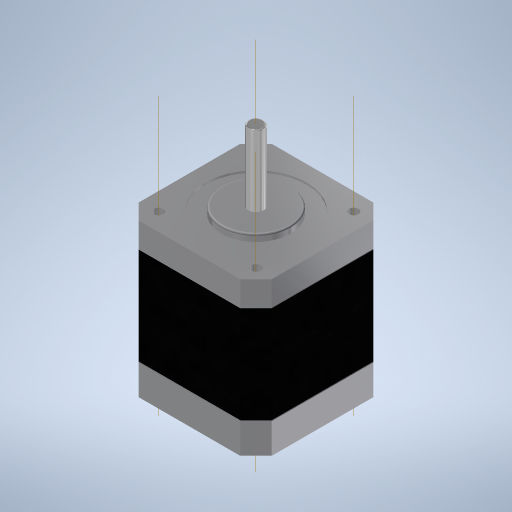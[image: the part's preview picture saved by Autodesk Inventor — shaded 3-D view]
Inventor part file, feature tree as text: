
AUTODESK INVENTOR PART (.ipt)
format: ipt  version: 2024 (Build 280153000, 153)  size: 359,424 bytes
history: native  units: mm
features: extrude x6, other x5, fillet x4, sketch x1
ambient origin geometry x8: Origin, YZ Plane, XZ Plane, XY Plane, X Axis, Y Axis, Z Axis, Center Point
bodies: Solid1 (feature_tree)
feature tree (16):
  extrude  "Extrusion1"  Depth=5.0mm
  fillet  "Fillet1"  Radius=5.0mm
  extrude  "Extrusion2"  Depth=42.2mm
  fillet  "Fillet2"  Radius=21.1mm
  extrude  "Extrusion3"  Depth=42.2mm
  extrude  "Extrusion4"  Depth=42.2mm
  extrude  "Extrusion5"  Depth=42.2mm
  fillet  "Fillet3"  Radius=3.0mm
  extrude  "Extrusion6"  Depth=31.0mm
  fillet  "Fillet4"  Radius=31.0mm
  other  "Work Axis1"
  other  "Work Axis2"
  other  "Work Axis3"
  other  "Work Axis4"
  other  "Work Axis5"
  sketch  "Sketch1"  dims[d8=5.0mm d9=5.0mm d10=5.0mm d11=21.1mm d12=21.1mm d13=3.0mm d14=3.0mm d15=3.0mm d16=3.0mm d17=31.0mm d18=31.0mm d19=31.0mm d20=31.0mm d21=5.6mm d22=5.6mm d23=9.8mm d24=0.0mm d25=0.25mm d26=31.0mm d27=0.0mm d28=0.25mm d29=7.75mm d30=0.0mm d31=32.0mm d33=0.6mm d34=0.0mm d35=22.0mm d37=2.2mm d38=0.0mm d39=0.5mm d40=22.5mm d41=0.0mm d42=0.5mm d43=5.6mm d44=5.6mm d45=5.6mm d46=5.6mm d47=42.2mm]
